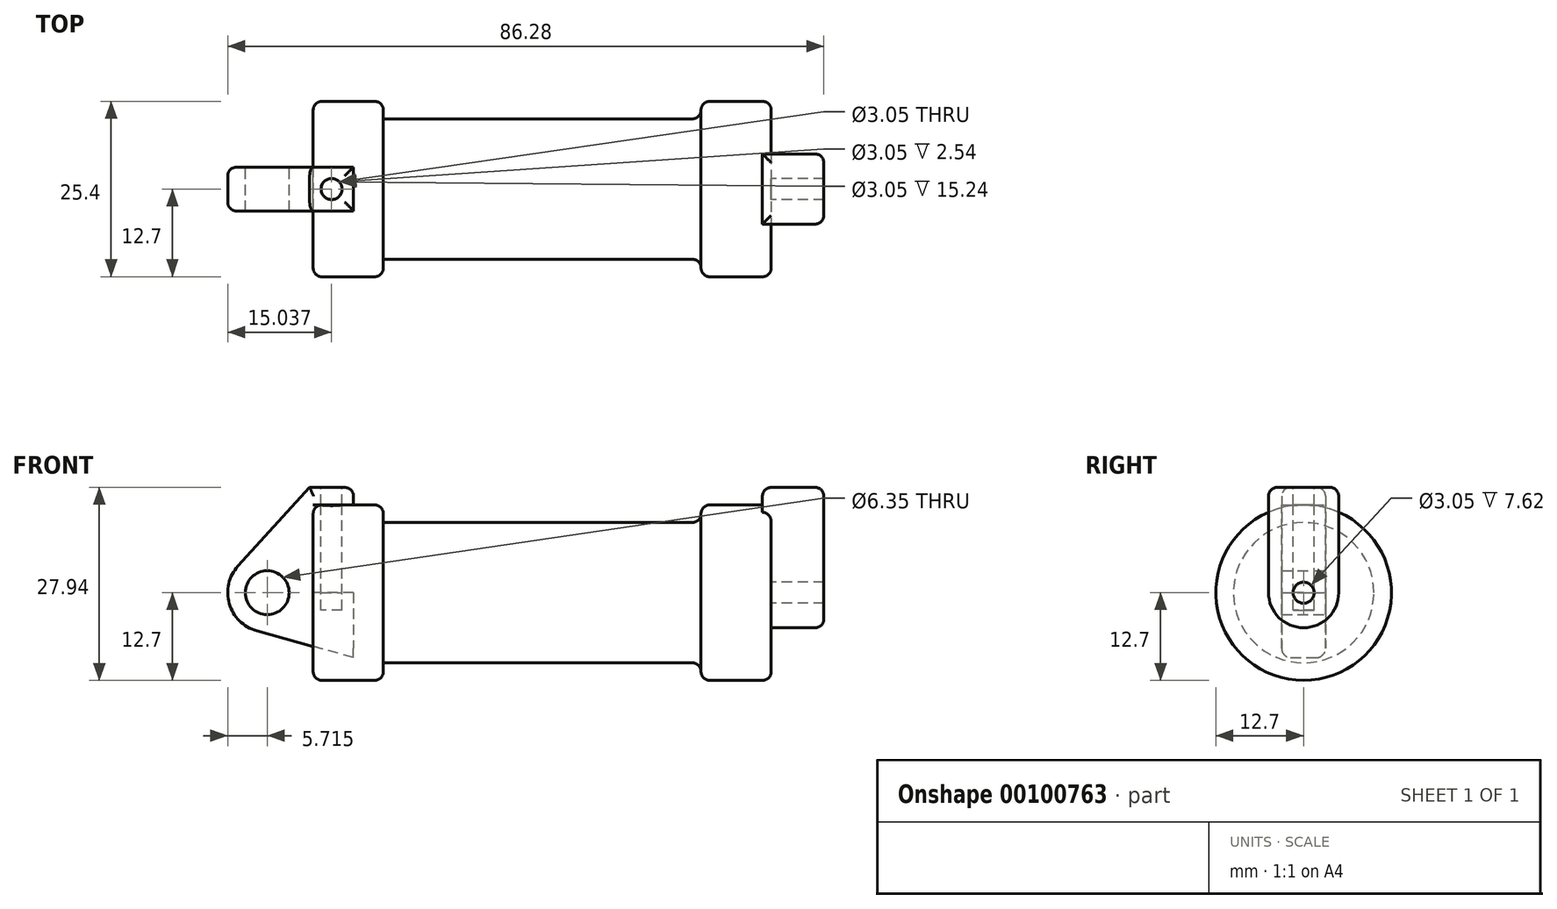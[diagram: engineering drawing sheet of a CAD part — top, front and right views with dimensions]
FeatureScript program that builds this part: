
annotation { "Feature Type Name" : "Feature", "Feature Type Description" : "" }
export const myFeature = defineFeature(function(context is Context, id is Id, definition is map)
    precondition{}
    {
        {
            var Q0;
            Q0=qCreatedBy(makeId("Front.planeOp"),FACE);
            var sketch = newSketch(context, id + "F0", { "sketchPlane" : qUnion([Q0])});
            skLineSegment(sketch, "E0", {"start": v(0, 0) * mm, "end": v(0, 12.7) * mm});
            skLineSegment(sketch, "E1", {"start": v(0, 12.7) * mm, "end": v(10.16, 12.7) * mm});
            skLineSegment(sketch, "E2", {"start": v(10.16, 12.7) * mm, "end": v(10.16, 10.16) * mm});
            skLineSegment(sketch, "E3", {"start": v(10.16, 10.16) * mm, "end": v(56.13, 10.16) * mm});
            skLineSegment(sketch, "E4", {"start": v(56.13, 10.16) * mm, "end": v(56.13, 12.7) * mm});
            skLineSegment(sketch, "E5", {"start": v(56.13, 12.7) * mm, "end": v(66.3, 12.7) * mm});
            skLineSegment(sketch, "E6", {"start": v(66.3, 12.7) * mm, "end": v(66.3, 0) * mm});
            skLineSegment(sketch, "E7", {"start": v(66.3, 0) * mm, "end": v(0, 0) * mm});
            skLineSegment(sketch, "E8", {"start": v(5.84, 15.24) * mm, "end": v(-0.5, 15.24) * mm});
            skLineSegment(sketch, "E9", {"start": v(-0.5, 15.24) * mm, "end": v(-10.88, 3.85) * mm});
            skLineSegment(sketch, "E10", {"start": v(0, 0) * mm, "end": v(-6.65, 0) * mm});
            skCircle(sketch, "E11", {"center": v(-6.65, 0) * mm, "radius": 5.72 * mm});
            skCircle(sketch, "E12", {"center": v(-6.65, 0) * mm, "radius": 3.18 * mm});
            skLineSegment(sketch, "E13", {"start": v(5.84, 15.24) * mm, "end": v(5.84, -9.4) * mm});
            skLineSegment(sketch, "E14", {"start": v(5.84, -9.4) * mm, "end": v(-8.18, -5.5) * mm});
            skSolve(sketch);
        }
        {
            var Q0;
            {var subQ0=sQuery(id+"F0.wireOp",EDGE,"E2");Q0=makeQuery(id+"F0.imprint","IMPRINT",FACE,{"disambiguationData":[TD([[makeQuery(id+"F0.imprint","IMPRINT",EDGE,{"derivedFrom":subQ0}),-1.0]])]});}
            var Q1;
            {var subQ0=sQuery(id+"F0.wireOp",EDGE,"E0");Q1=makeQuery(id+"F0.imprint","IMPRINT",FACE,{"disambiguationData":[TD([[makeQuery(id+"F0.imprint","IMPRINT",EDGE,{"derivedFrom":subQ0}),-1.0]])]});}
            var Q2;
            Q2=sQuery(id+"F0.wireOp",EDGE,"E7");
            revolve(context, id + "F1", {"entities" : qUnion([Q0, Q1]), "axis" : qUnion([Q2]), "revolveType" : RevolveType.FULL});
        }
        {
            var Q0;
            {var subQ3=sQuery(id+"F0.wireOp",EDGE,"E0");Q0=makeQuery(id+"F0.imprint","IMPRINT",FACE,{"disambiguationData":[TD([[makeQuery(id+"F0.imprint","IMPRINT",EDGE,{"derivedFrom":subQ3}),1.0]])]});}
            var Q1;
            {var subQ4=sQuery(id+"F0.wireOp",EDGE,"E12");Q1=makeQuery(id+"F0.imprint","IMPRINT",FACE,{"disambiguationData":[TD([[makeQuery(id+"F0.imprint","IMPRINT",EDGE,{"derivedFrom":subQ4}),-1.0]])]});}
            var Q2;
            {var subQ0=sQuery(id+"F0.wireOp",EDGE,"E14");Q2=makeQuery(id+"F0.imprint","IMPRINT",FACE,{"disambiguationData":[TD([[makeQuery(id+"F0.imprint","IMPRINT",EDGE,{"derivedFrom":subQ0}),-1.0]])]});}
            extrude(context, id + "F2", {"entities" : qUnion([Q0, Q1, Q2]), "endBound" : BoundingType.SYMMETRIC, "depth" : 6.35 * mm});
        }
        {
            var Q0;
            Q0=makeQuery(id+"F1.opRevolve","SWEPT_FACE",FACE,{"disambiguationData":[OSD([sQuery(id+"F0.wireOp",EDGE,"E6")])]});
            var sketch = newSketch(context, id + "F3", { "sketchPlane" : qUnion([Q0])});
            skCircle(sketch, "E15", {"center": v(0, 0) * mm, "radius": 5.08 * mm});
            skCircle(sketch, "E16", {"center": v(0, 0) * mm, "radius": 1.52 * mm});
            skLineSegment(sketch, "E17", {"start": v(-5.08, 0) * mm, "end": v(-5.08, 15.24) * mm});
            skLineSegment(sketch, "E18", {"start": v(5.08, 15.24) * mm, "end": v(5.08, 0) * mm});
            skLineSegment(sketch, "E19.0", {"start": v(-3.18, 15.24) * mm, "end": v(3.17, 15.24) * mm});
            skLineSegment(sketch, "E20", {"start": v(-5.08, 15.24) * mm, "end": v(5.08, 15.24) * mm});
            skSolve(sketch);
        }
        {
            var Q0;
            {var subQ0=sQuery(id+"F3.wireOp",EDGE,"E20");var subQ1=sQuery(id+"F3.wireOp",EDGE,"E17");var subQ2=makeQuery(id+"F3.imprint","INTERSECT",VERTEX,{"derivedFrom":[subQ1,subQ0]});Q0=makeQuery(id+"F3.imprint","IMPRINT",FACE,{"disambiguationData":[TD([[makeQuery(id+"F3.imprint","IMPRINT",EDGE,{"disambiguationData":[TD([[subQ2,-1.0]])],"derivedFrom":subQ0}),-1.0]])]});}
            var Q1;
            {var subQ0=sQuery(id+"F3.wireOp",EDGE,"E17");var subQ1=sQuery(id+"F3.wireOp",EDGE,"E15");var subQ2=makeQuery(id+"F3.imprint","INTERSECT",VERTEX,{"derivedFrom":[subQ1,subQ0]});Q1=makeQuery(id+"F3.imprint","IMPRINT",FACE,{"disambiguationData":[TD([[makeQuery(id+"F3.imprint","IMPRINT",EDGE,{"disambiguationData":[TD([[subQ2,1.0]])],"derivedFrom":subQ1}),-1.0]])]});}
            var Q2;
            Q2=makeQuery(id+"F3.imprint","IMPRINT",FACE,{"disambiguationData":[TD([[makeQuery(id+"F3.imprint","IMPRINT",EDGE,{"derivedFrom":sQuery(id+"F3.wireOp",EDGE,"E16")}),-1.0]])]});
            extrude(context, id + "F4", {"entities" : qUnion([Q0, Q1, Q2]), "operationType" : NewBodyOperationType.ADD, "depth" : 7.62 * mm, "hasSecondDirection" : true, "secondDirectionOppositeDirection" : true, "secondDirectionDepth" : 1.27 * mm});
        }
        {
            var Q0;
            Q0=makeQuery(id+"F4.opExtrude","SWEPT_FACE",FACE,{"disambiguationData":[OSD([sQuery(id+"F3.wireOp",EDGE,"E20")])]});
            var sketch = newSketch(context, id + "F5", { "sketchPlane" : qUnion([Q0])});
            skCircle(sketch, "E21", {"center": v(2.67, 0) * mm, "radius": 1.52 * mm});
            skLineSegment(sketch, "E22", {"start": v(65.02, 0) * mm, "end": v(73.91, 0) * mm});
            skCircle(sketch, "E23", {"center": v(69.47, 0) * mm, "radius": 1.52 * mm});
            skSolve(sketch);
        }
        {
            var Q0;
            Q0=makeQuery(id+"F5.imprint","IMPRINT",FACE,{"disambiguationData":[TD([[makeQuery(id+"F5.imprint","IMPRINT",EDGE,{"derivedFrom":sQuery(id+"F5.wireOp",EDGE,"E21")}),1.0]])]});
            extrude(context, id + "F6", {"entities" : qUnion([Q0]), "operationType" : NewBodyOperationType.REMOVE, "oppositeDirection" : true, "depth" : 17.78 * mm});
        }
        {
            var Q0;
            {var subQ0=sQuery(id+"F5.wireOp",EDGE,"E23");var subQ1=sQuery(id+"F5.wireOp",EDGE,"E22");var subQ2=makeQuery(id+"F5.imprint","INTERSECT",VERTEX,{"disambiguationData":[OD(0.0)],"derivedFrom":[subQ1,subQ0]});Q0=makeQuery(id+"F5.imprint","IMPRINT",FACE,{"disambiguationData":[TD([[makeQuery(id+"F5.imprint","IMPRINT",EDGE,{"disambiguationData":[TD([[subQ2,-1.0]])],"derivedFrom":subQ1}),-1.0]])]});}
            var Q1;
            {var subQ0=sQuery(id+"F5.wireOp",EDGE,"E23");var subQ1=sQuery(id+"F5.wireOp",EDGE,"E22");var subQ2=makeQuery(id+"F5.imprint","INTERSECT",VERTEX,{"disambiguationData":[OD(0.0)],"derivedFrom":[subQ1,subQ0]});Q1=makeQuery(id+"F5.imprint","IMPRINT",FACE,{"disambiguationData":[TD([[makeQuery(id+"F5.imprint","IMPRINT",EDGE,{"disambiguationData":[TD([[subQ2,-1.0]])],"derivedFrom":subQ1}),1.0]])]});}
            extrude(context, id + "F7", {"entities" : qUnion([Q0, Q1]), "operationType" : NewBodyOperationType.ADD, "oppositeDirection" : true, "depth" : 10.4 * mm});
        }
        {
            var Q0;
            Q0=makeQuery(id+"F1.opRevolve","SWEPT_EDGE",EDGE,{"disambiguationData":[OSD([sQuery(id+"F0.wireOp",EDGE,"E1"),sQuery(id+"F0.wireOp",EDGE,"E2")])]});
            var Q1;
            Q1=makeQuery(id+"F1.opRevolve","SWEPT_EDGE",EDGE,{"disambiguationData":[OSD([sQuery(id+"F0.wireOp",EDGE,"E0"),sQuery(id+"F0.wireOp",EDGE,"E1")])]});
            var Q2;
            Q2=makeQuery(id+"F2.opExtrude","SWEPT_EDGE",EDGE,{"disambiguationData":[OSD([sQuery(id+"F0.wireOp",EDGE,"E8"),sQuery(id+"F0.wireOp",EDGE,"E13")])]});
            var Q3;
            Q3=makeQuery(id+"F2.opExtrude","CAP_EDGE",EDGE,{"disambiguationData":[OSD([sQuery(id+"F0.wireOp",EDGE,"E8")])],"isStart":false});
            var Q4;
            Q4=makeQuery(id+"F2.opExtrude","CAP_EDGE",EDGE,{"disambiguationData":[OSD([sQuery(id+"F0.wireOp",EDGE,"E8")])],"isStart":true});
            var Q5;
            Q5=makeQuery(id+"F2.opExtrude","CAP_EDGE",EDGE,{"disambiguationData":[OSD([sQuery(id+"F0.wireOp",EDGE,"E9")])],"isStart":false});
            var Q6;
            Q6=makeQuery(id+"F2.opExtrude","CAP_EDGE",EDGE,{"disambiguationData":[OSD([sQuery(id+"F0.wireOp",EDGE,"E9")])],"isStart":true});
            var Q7;
            Q7=makeQuery(id+"F1.opRevolve","SWEPT_EDGE",EDGE,{"disambiguationData":[OSD([sQuery(id+"F0.wireOp",EDGE,"E5"),sQuery(id+"F0.wireOp",EDGE,"E6")])]});
            var Q8;
            Q8=makeQuery(id+"F1.opRevolve","SWEPT_FACE",FACE,{"disambiguationData":[OSD([sQuery(id+"F0.wireOp",EDGE,"E4")])]});
            var Q9;
            Q9=makeQuery(id+"F4.opExtrude","CAP_EDGE",EDGE,{"disambiguationData":[OSD([sQuery(id+"F3.wireOp",EDGE,"E18")])],"isStart":false});
            var Q10;
            Q10=makeQuery(id+"F4.opExtrude","CAP_EDGE",EDGE,{"disambiguationData":[OSD([sQuery(id+"F3.wireOp",EDGE,"E20")])],"isStart":false});
            var Q11;
            Q11=makeQuery(id+"F4.opExtrude","SWEPT_EDGE",EDGE,{"disambiguationData":[OSD([sQuery(id+"F3.wireOp",EDGE,"E18"),sQuery(id+"F3.wireOp",EDGE,"E20")])]});
            var Q12;
            Q12=makeQuery(id+"F4.opExtrude","CAP_EDGE",EDGE,{"disambiguationData":[OSD([sQuery(id+"F3.wireOp",EDGE,"E20")])],"isStart":true});
            var Q13;
            Q13=makeQuery(id+"F4.opExtrude","SWEPT_EDGE",EDGE,{"disambiguationData":[OSD([sQuery(id+"F3.wireOp",EDGE,"E17"),sQuery(id+"F3.wireOp",EDGE,"E20")])]});
            fillet(context, id + "F8", {"entities" : qUnion([Q0, Q1, Q2, Q3, Q4, Q5, Q6, Q7, Q8, Q9, Q10, Q11, Q12, Q13]), "radius" : 1.27 * mm, "tangentPropagation" : true, "allowEdgeOverflow" : false});
        }
    });
